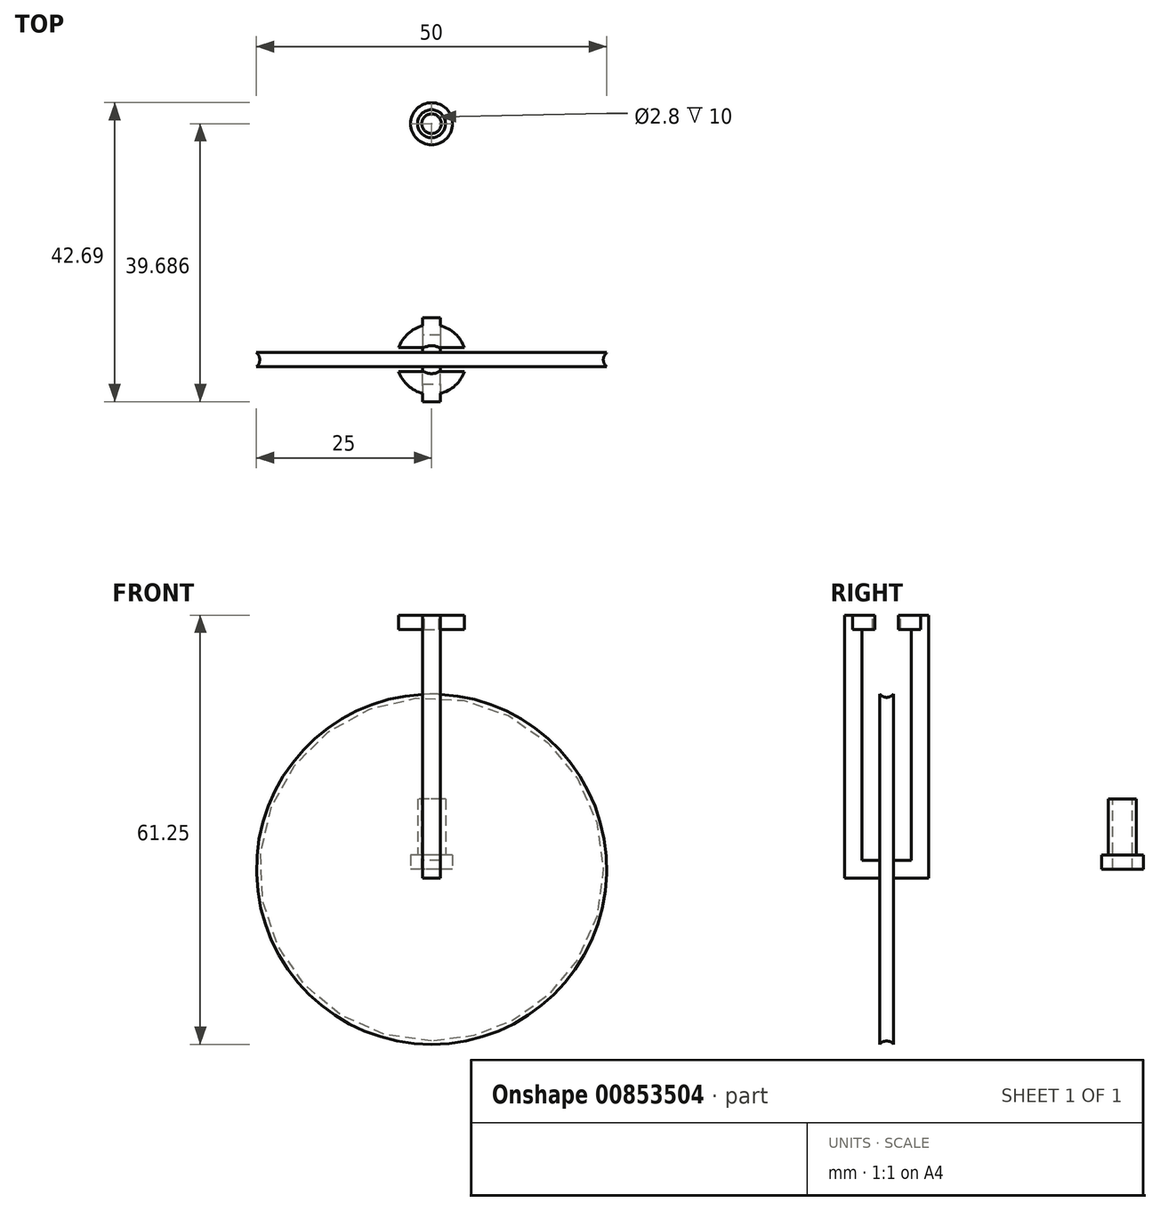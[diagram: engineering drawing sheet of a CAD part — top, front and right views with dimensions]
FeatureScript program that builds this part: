
annotation { "Feature Type Name" : "Feature", "Feature Type Description" : "" }
export const myFeature = defineFeature(function(context is Context, id is Id, definition is map)
    precondition{}
    {
        {
            var Q0;
            Q0=qCreatedBy(makeId("Front.planeOp"),FACE);
            var sketch = newSketch(context, id + "F0", { "sketchPlane" : qUnion([Q0])});
            skCircle(sketch, "E0", {"center": v(0, 0) * mm, "radius": 25 * mm});
            skSolve(sketch);
        }
        {
            var Q0;
            Q0 = qSketchRegion(id + "F0", true);
            extrude(context, id + "F1", {"entities" : qUnion([Q0]), "endBound" : BoundingType.SYMMETRIC, "depth" : 2 * mm, "offsetDistance" : 25 * mm});
        }
        {
            var Q0;
            Q0=qCreatedBy(makeId("Right.planeOp"),FACE);
            var sketch = newSketch(context, id + "F2", { "sketchPlane" : qUnion([Q0])});
            skArc(sketch, "E1", {"start": v(1, -25) * mm, "mid": v(0, -24.53) * mm, "end": v(-1, -25) * mm});
            skLineSegment(sketch, "E2", {"start": v(-1, -25) * mm, "end": v(1, -25) * mm});
            skLineSegment(sketch, "E3", {"start": v(7.37, 0) * mm, "end": v(-7.8, 0) * mm});
            skSolve(sketch);
        }
        {
            var Q0;
            Q0=makeQuery(id+"F2.imprint","IMPRINT",FACE,{"disambiguationData":[TD([[makeQuery(id+"F2.imprint","IMPRINT",EDGE,{"derivedFrom":sQuery(id+"F2.wireOp",EDGE,"E1")}),1.0]])]});
            var Q1;
            Q1=sQuery(id+"F2.wireOp",EDGE,"E3");
            revolve(context, id + "F3", {"operationType" : NewBodyOperationType.REMOVE, "surfaceOperationType" : NewSurfaceOperationType.NEW, "entities" : qUnion([Q0]), "axis" : qUnion([Q1]), "revolveType" : RevolveType.FULL, "oppositeDirection" : true});
        }
        {
            var Q0;
            Q0=makeQuery(id+"F1.opExtrude","CAP_FACE",FACE,{"disambiguationData":[OSD([sQuery(id+"F0.wireOp",EDGE,"E0")])],"isStart":true});
            var sketch = newSketch(context, id + "F4", { "sketchPlane" : qUnion([Q0])});
            skLineSegment(sketch, "E4.bottom", {"start": v(1.25, -1.25) * mm, "end": v(-1.25, -1.25) * mm});
            skLineSegment(sketch, "E4.top", {"start": v(1.25, 1.25) * mm, "end": v(-1.25, 1.25) * mm});
            skLineSegment(sketch, "E4.left", {"start": v(1.25, -1.25) * mm, "end": v(1.25, 1.25) * mm});
            skLineSegment(sketch, "E4.right", {"start": v(-1.25, -1.25) * mm, "end": v(-1.25, 1.25) * mm});
            skPoint(sketch, "E4.middle", {"position": v(0, 0) * mm});
            skSolve(sketch);
        }
        {
            var Q0;
            Q0 = qSketchRegion(id + "F4", true);
            extrude(context, id + "F5", {"entities" : qUnion([Q0]), "operationType" : NewBodyOperationType.ADD, "depth" : 5 * mm, "offsetDistance" : 25 * mm});
        }
        {
            var Q0;
            Q0=makeQuery(id+"F5.opExtrude","SWEPT_FACE",FACE,{"disambiguationData":[OSD([sQuery(id+"F4.wireOp",EDGE,"E4.top")])]});
            var sketch = newSketch(context, id + "F6", { "sketchPlane" : qUnion([Q0])});
            skLineSegment(sketch, "E5.bottom", {"start": v(1.25, 6) * mm, "end": v(-1.25, 6) * mm});
            skLineSegment(sketch, "E5.top", {"start": v(1.25, 3.5) * mm, "end": v(-1.25, 3.5) * mm});
            skLineSegment(sketch, "E5.left", {"start": v(1.25, 6) * mm, "end": v(1.25, 3.5) * mm});
            skLineSegment(sketch, "E5.right", {"start": v(-1.25, 6) * mm, "end": v(-1.25, 3.5) * mm});
            skSolve(sketch);
        }
        {
            var Q0;
            Q0 = qSketchRegion(id + "F6", true);
            extrude(context, id + "F7", {"entities" : qUnion([Q0]), "operationType" : NewBodyOperationType.ADD, "depth" : 35 * mm, "offsetDistance" : 25 * mm});
        }
        {
            var Q0;
            Q0=makeQuery(id+"F1.opExtrude","SWEPT_BODY",BODY,{"disambiguationData":[OSD([sQuery(id+"F0.wireOp",EDGE,"E0")])]});
            var Q1;
            Q1=qCreatedBy(makeId("Front.planeOp"),FACE);
            mirror(context, id + "F8", {"operationType" : NewBodyOperationType.ADD, "entities" : qUnion([Q0]), "mirrorPlane" : qUnion([Q1])});
        }
        {
            var Q0;
            Q0=makeQuery(id+"F7.opExtrude","CAP_FACE",FACE,{"disambiguationData":[OSD([sQuery(id+"F6.wireOp",EDGE,"E5.bottom"),sQuery(id+"F6.wireOp",EDGE,"E5.top"),sQuery(id+"F6.wireOp",EDGE,"E5.left"),sQuery(id+"F6.wireOp",EDGE,"E5.right")])],"isStart":false});
            var sketch = newSketch(context, id + "F9", { "sketchPlane" : qUnion([Q0])});
            skCircle(sketch, "E6", {"center": v(0, 0) * mm, "radius": 5 * mm});
            skCircle(sketch, "E7", {"center": v(0, 0) * mm, "radius": 2 * mm});
            skSolve(sketch);
        }
        {
            var Q0;
            Q0 = qSketchRegion(id + "F9", true);
            extrude(context, id + "F10", {"entities" : qUnion([Q0]), "operationType" : NewBodyOperationType.ADD, "oppositeDirection" : true, "depth" : 2 * mm, "offsetDistance" : 25 * mm});
        }
        {
            var Q0;
            Q0=qCreatedBy(makeId("Top.planeOp"),FACE);
            var sketch = newSketch(context, id + "F11", { "sketchPlane" : qUnion([Q0])});
            skCircle(sketch, "E8", {"center": v(0, 33.69) * mm, "radius": 3 * mm});
            skCircle(sketch, "E9", {"center": v(0, 33.69) * mm, "radius": 2 * mm});
            skSolve(sketch);
        }
        {
            var Q0;
            Q0=makeQuery(id+"F11.imprint","IMPRINT",FACE,{"disambiguationData":[TD([[makeQuery(id+"F11.imprint","IMPRINT",EDGE,{"derivedFrom":sQuery(id+"F11.wireOp",EDGE,"E9")}),1.0]])]});
            extrude(context, id + "F12", {"entities" : qUnion([Q0]), "depth" : 10 * mm, "offsetDistance" : 25 * mm});
        }
        {
            var Q0;
            Q0 = qSketchRegion(id + "F11", true);
            extrude(context, id + "F13", {"entities" : qUnion([Q0]), "operationType" : NewBodyOperationType.ADD, "depth" : 2 * mm, "offsetDistance" : 25 * mm});
        }
        {
            var Q0;
            Q0=makeQuery(id+"F12.opExtrude","CAP_FACE",FACE,{"disambiguationData":[OSD([sQuery(id+"F11.wireOp",EDGE,"E9")])],"isStart":false});
            var sketch = newSketch(context, id + "F14", { "sketchPlane" : qUnion([Q0])});
            skCircle(sketch, "E10", {"center": v(0, 33.69) * mm, "radius": 1.4 * mm});
            skSolve(sketch);
        }
        {
            var Q0;
            Q0=makeQuery(id+"F14.imprint","IMPRINT",FACE,{"disambiguationData":[TD([[makeQuery(id+"F14.imprint","IMPRINT",EDGE,{"derivedFrom":sQuery(id+"F14.wireOp",EDGE,"E10")}),1.0]])]});
            extrude(context, id + "F15", {"entities" : qUnion([Q0]), "operationType" : NewBodyOperationType.REMOVE, "endBound" : BoundingType.THROUGH_ALL, "oppositeDirection" : true, "depth" : 2 * mm, "offsetDistance" : 25 * mm});
        }
        {
            var Q0;
            {var subQ0=makeQuery(id+"F7.opExtrude","CAP_FACE",FACE,{"disambiguationData":[OSD([sQuery(id+"F6.wireOp",EDGE,"E5.bottom"),sQuery(id+"F6.wireOp",EDGE,"E5.top"),sQuery(id+"F6.wireOp",EDGE,"E5.left"),sQuery(id+"F6.wireOp",EDGE,"E5.right")])],"isStart":false});Q0=makeQuery(id+"F10.boolean.opBoolean","MERGE",FACE,{"derivedFrom":[subQ0,makeQuery(id+"F8.opPattern","COPY",FACE,{"derivedFrom":subQ0,"instanceName":"1"}),makeQuery(id+"F10.opExtrude","CAP_FACE",FACE,{"disambiguationData":[OSD([sQuery(id+"F9.wireOp",EDGE,"E6"),sQuery(id+"F9.wireOp",EDGE,"E7")])],"isStart":true})]});}
            var sketch = newSketch(context, id + "F16", { "sketchPlane" : qUnion([Q0])});
            skLineSegment(sketch, "E11.bottom", {"start": v(7.5, 1.7) * mm, "end": v(-7.5, 1.7) * mm});
            skLineSegment(sketch, "E11.top", {"start": v(7.5, -1.7) * mm, "end": v(-7.5, -1.7) * mm});
            skLineSegment(sketch, "E11.left", {"start": v(7.5, 1.7) * mm, "end": v(7.5, -1.7) * mm});
            skLineSegment(sketch, "E11.right", {"start": v(-7.5, 1.7) * mm, "end": v(-7.5, -1.7) * mm});
            skPoint(sketch, "E11.middle", {"position": v(0, 0) * mm});
            skSolve(sketch);
        }
        {
            var Q0;
            Q0 = qSketchRegion(id + "F16", true);
            extrude(context, id + "F17", {"entities" : qUnion([Q0]), "operationType" : NewBodyOperationType.REMOVE, "oppositeDirection" : true, "depth" : 5 * mm, "offsetDistance" : 25 * mm});
        }
    });
